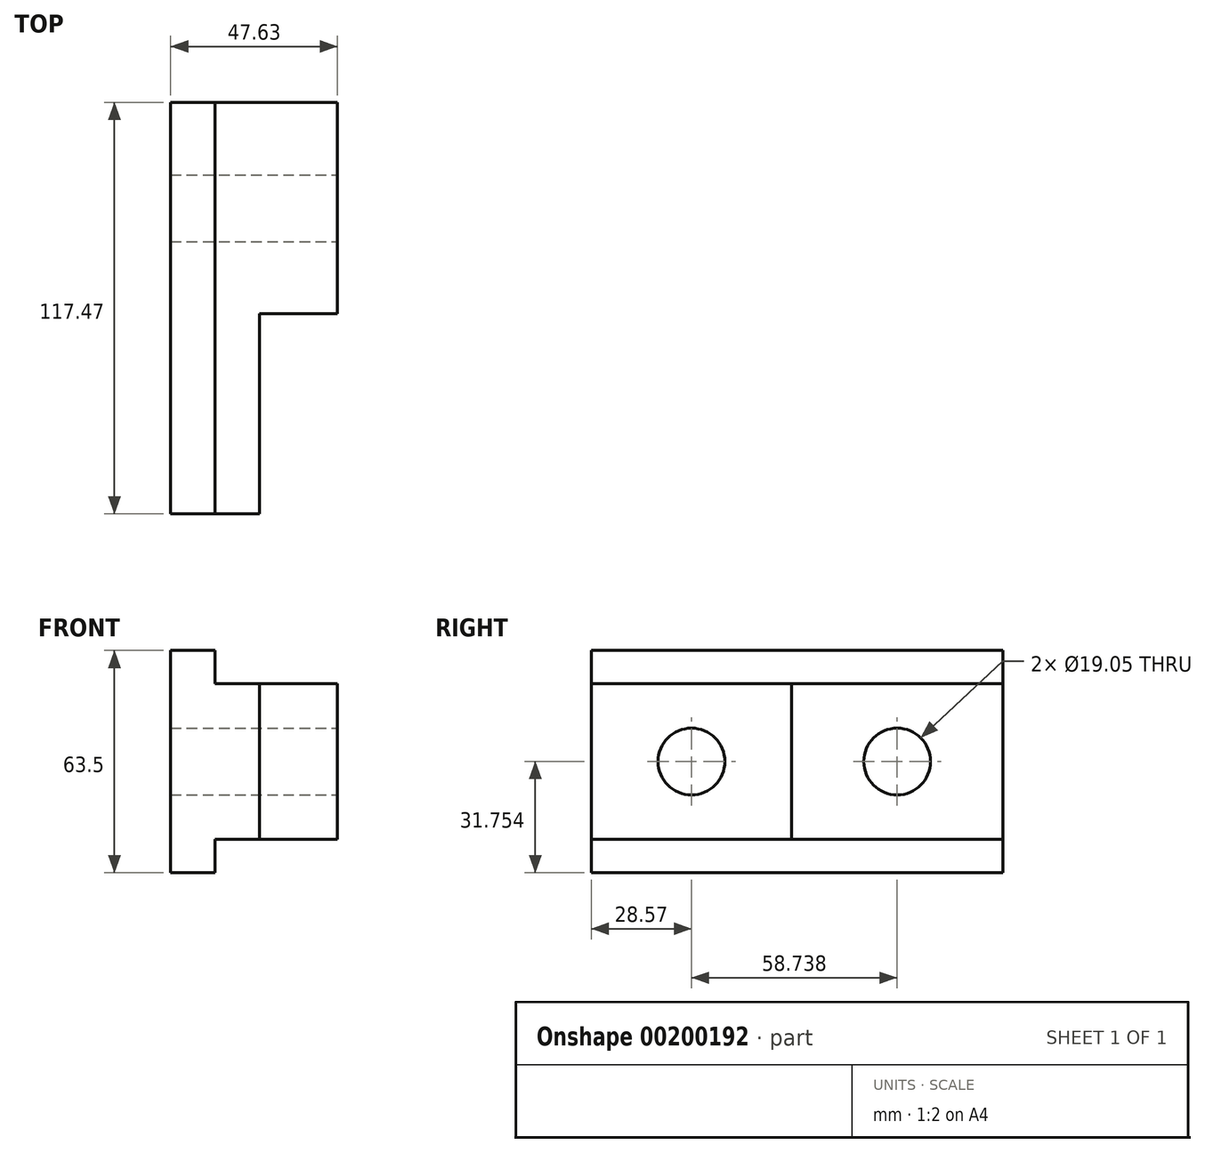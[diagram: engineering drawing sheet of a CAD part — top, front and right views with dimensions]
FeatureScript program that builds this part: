
annotation { "Feature Type Name" : "Feature", "Feature Type Description" : "" }
export const myFeature = defineFeature(function(context is Context, id is Id, definition is map)
    precondition{}
    {
        {
            var Q0;
            Q0=qCreatedBy(makeId("Front.planeOp"),FACE);
            var sketch = newSketch(context, id + "F0", { "sketchPlane" : qUnion([Q0])});
            skLineSegment(sketch, "E0", {"start": v(-712.36, 373.36) * mm, "end": v(-712.36, 309.86) * mm});
            skLineSegment(sketch, "E1", {"start": v(-712.36, 373.36) * mm, "end": v(-699.66, 373.36) * mm});
            skLineSegment(sketch, "E2", {"start": v(-712.36, 309.86) * mm, "end": v(-699.66, 309.86) * mm});
            skLineSegment(sketch, "E3", {"start": v(-699.66, 309.86) * mm, "end": v(-699.66, 319.39) * mm});
            skLineSegment(sketch, "E4", {"start": v(-699.66, 373.36) * mm, "end": v(-699.66, 363.84) * mm});
            skLineSegment(sketch, "E5", {"start": v(-699.66, 319.39) * mm, "end": v(-664.73, 319.39) * mm});
            skLineSegment(sketch, "E6", {"start": v(-699.66, 363.84) * mm, "end": v(-664.73, 363.84) * mm});
            skLineSegment(sketch, "E7", {"start": v(-664.73, 363.84) * mm, "end": v(-664.73, 319.39) * mm});
            skSolve(sketch);
        }
        {
            var Q0;
            Q0 = qSketchRegion(id + "F0", true);
            extrude(context, id + "F1", {"entities" : qUnion([Q0]), "depth" : 117.47 * mm});
        }
        {
            var Q0;
            Q0=makeQuery(id+"F1.opExtrude","SWEPT_FACE",FACE,{"disambiguationData":[OSD([sQuery(id+"F0.wireOp",EDGE,"E7")])]});
            var sketch = newSketch(context, id + "F2", { "sketchPlane" : qUnion([Q0])});
            skLineSegment(sketch, "E8", {"start": v(-117.48, 363.84) * mm, "end": v(-60.33, 363.84) * mm});
            skLineSegment(sketch, "E9", {"start": v(-60.33, 363.84) * mm, "end": v(-60.33, 319.39) * mm});
            skLineSegment(sketch, "E10", {"start": v(-60.33, 319.39) * mm, "end": v(-117.48, 319.39) * mm});
            skLineSegment(sketch, "E11", {"start": v(-117.48, 319.39) * mm, "end": v(-117.48, 363.84) * mm});
            skSolve(sketch);
        }
        {
            var Q0;
            Q0=makeQuery(id+"F2.imprint","IMPRINT",FACE,{"disambiguationData":[TD([[makeQuery(id+"F2.imprint","IMPRINT",EDGE,{"derivedFrom":sQuery(id+"F2.wireOp",EDGE,"E8")}),-1.0]])]});
            extrude(context, id + "F3", {"entities" : qUnion([Q0]), "operationType" : NewBodyOperationType.REMOVE, "oppositeDirection" : true, "depth" : 22.22 * mm});
        }
        {
            var Q0;
            Q0=makeQuery(id+"F3.boolean.opBoolean","COPY",FACE,{"derivedFrom":makeQuery(id+"F3.opExtrude","CAP_FACE",FACE,{"disambiguationData":[OSD([sQuery(id+"F2.wireOp",EDGE,"E8"),sQuery(id+"F2.wireOp",EDGE,"E9"),sQuery(id+"F2.wireOp",EDGE,"E10"),sQuery(id+"F2.wireOp",EDGE,"E11")])],"isStart":false})});
            var sketch = newSketch(context, id + "F4", { "sketchPlane" : qUnion([Q0])});
            skCircle(sketch, "E12", {"center": v(-88.9, 341.61) * mm, "radius": 9.53 * mm});
            skPoint(sketch, "E12.centerSnap0", {"position": v(-117.48, 341.61) * mm});
            skPoint(sketch, "E12.centerSnap1", {"position": v(-88.9, 363.84) * mm});
            skSolve(sketch);
        }
        {
            var Q0;
            Q0=makeQuery(id+"F4.imprint","IMPRINT",FACE,{"disambiguationData":[TD([[makeQuery(id+"F4.imprint","IMPRINT",EDGE,{"derivedFrom":sQuery(id+"F4.wireOp",EDGE,"E12")}),1.0]])]});
            extrude(context, id + "F5", {"entities" : qUnion([Q0]), "operationType" : NewBodyOperationType.REMOVE, "endBound" : BoundingType.THROUGH_ALL, "oppositeDirection" : true, "depth" : 25.4 * mm});
        }
        {
            var Q0;
            Q0=makeQuery(id+"F1.opExtrude","SWEPT_FACE",FACE,{"disambiguationData":[OSD([sQuery(id+"F0.wireOp",EDGE,"E7")])]});
            var sketch = newSketch(context, id + "F6", { "sketchPlane" : qUnion([Q0])});
            skCircle(sketch, "E13", {"center": v(-30.16, 341.61) * mm, "radius": 9.53 * mm});
            skPoint(sketch, "E13.centerSnap0", {"position": v(0, 341.61) * mm});
            skPoint(sketch, "E13.centerSnap1", {"position": v(-30.16, 363.84) * mm});
            skSolve(sketch);
        }
        {
            var Q0;
            Q0 = qSketchRegion(id + "F6", true);
            extrude(context, id + "F7", {"entities" : qUnion([Q0]), "operationType" : NewBodyOperationType.REMOVE, "endBound" : BoundingType.THROUGH_ALL, "oppositeDirection" : true, "depth" : 25.4 * mm});
        }
    });
